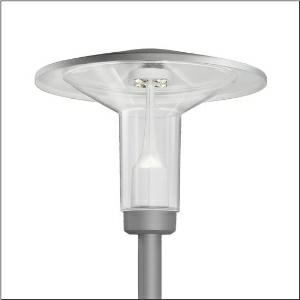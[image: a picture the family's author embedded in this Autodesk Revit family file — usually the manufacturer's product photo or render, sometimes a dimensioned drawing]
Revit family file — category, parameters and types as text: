
# Revit family: laterne_iq___st1_2a_5xa5255ef14h000022_800b
name_source: partatom
category: Lighting Fixtures
units: mm (PartAtom-declared; Revit-internal decimal feet)

## family parameters
Cut with Voids When Loaded = No
Host = Face
Light Source = No
Part Type = Normal
Room Calculation Point = No
Round Connector Dimension = Use Diameter
Shared = No

## types (1)
- --- (1 x LED, 1540 lm, 10.5 W, 3000K)
    Apparent Load = 11 VA
    CIE Flux Codes = 25 63 94 98 100
    Color Rendering = 70
    Color Temperature = 3000K
    Default Elevation = 1800 mm
    Description = Lantern iQ, mast luminaire, Module 540 iQ-SR, primary light control with 3 zone facetted reflector, of plastic, silver coated, highly specular, structured, primary optical cover: cover, of PMMA, transparent, light distribution: ST1.2a, light emission: direct distribution, primary light characteristic: asymmetric, installation type: post-top, LED, High Power LED, rated luminous flux: 1.540lm, luminous efficacy: 147lm/W, light colour: 730, colour temperature: 3000K, control gear: iQ Street-Remote, control: Street-Remote, Auto-Match, Temp-Guard, Lumen-Switch, Night-Set, Smart-Wire, Light-Fading, Desk-Remote (wireless, voltage-free reading and setting of iQ features in the workshop via application-optimized NFC function/RFID function), optimised constant luminous flux control (CLO 2.0), pre-setting: logarithmic dimming characteristic, mains connection: 230..240V, AC, 50/60Hz, connection cable pre-assembled, cable length: 5,5m, wiring characteristics: H07RN-F, start of lifetime: 11W, end of service life: 11W, reduction: 5W, luminaire housing, upper part, of glass-fibre reinforced polyester, coated, Siteco® metallic grey (DB 702S), diameter: 750mm, height: 583mm, spigot size: d x l = 76 x 70mm (post-top) | with reducer (optional accessory) 60 x 70mm, mounting height: 3..5m, post-top mast mounting element, of diecast aluminium, coated, Siteco® metallic grey (DB 702S), Module 540 iQ-SR, traffic white (RAL 9016), equipment: standard, protection rating (complete): IP65, insulation class (complete): insulation class II (safety insulation), certification: CE, ENEC, VDE, packaging unit: 1 piece

Light Distribution: ST1.2a
    Height = 583 mm
    Lamp = 1 x LED
    Lamp Light Flux = 1540 lm
    Lamp Power = 10.5 W
    Lamp count = 1
    Length = 750 mm
    Luminous efficacy = 147 lm/W
    Manufacturer = Siteco
    ModVariant = No
    Model = 5XA5255EF14H000022
    Number of Poles = 1
    OnlyDefault = Yes
    Power Factor = 1
    Product Name = Laterne iQ | ST1.2a
    Product group = mast luminaire | pylon top
    ProductGroupID = 6100
    Protection Class = Protection class II
    Protection Degree = IP 65
    RLX_Detail_Level = 1
    RLX_Emergency_Light_Flux = 0 lm
    RLX_Emergency_Type = 0
    RLX_Emergency_Type_DB = No
    RlxData = <blob elided: 33305 chars, md5=7b2021b2>
    Socket = socket
    Standby Power = 0 W
    System Light Flux = 1540 lm
    System Power = 11 W
    Type Comments = factory setting: luminous flux: 100 % | dim-lin: 254 | 419 mA
    Type Image = l_1006050.jpg
    URL = http://relux.com
    VarID = @adj_160596
    Voltage = 0 V
    Weight = 0.00 kg
    Width = 0 mm  [stored 0 ft]

note: [stored X ft] marks values corroborated as IEEE doubles in the binary element streams (Revit-internal decimal feet)

## geometry (parser evidence)
native form markers: Blend x4, Sweep x11
no freeform markers — native parametric forms only
